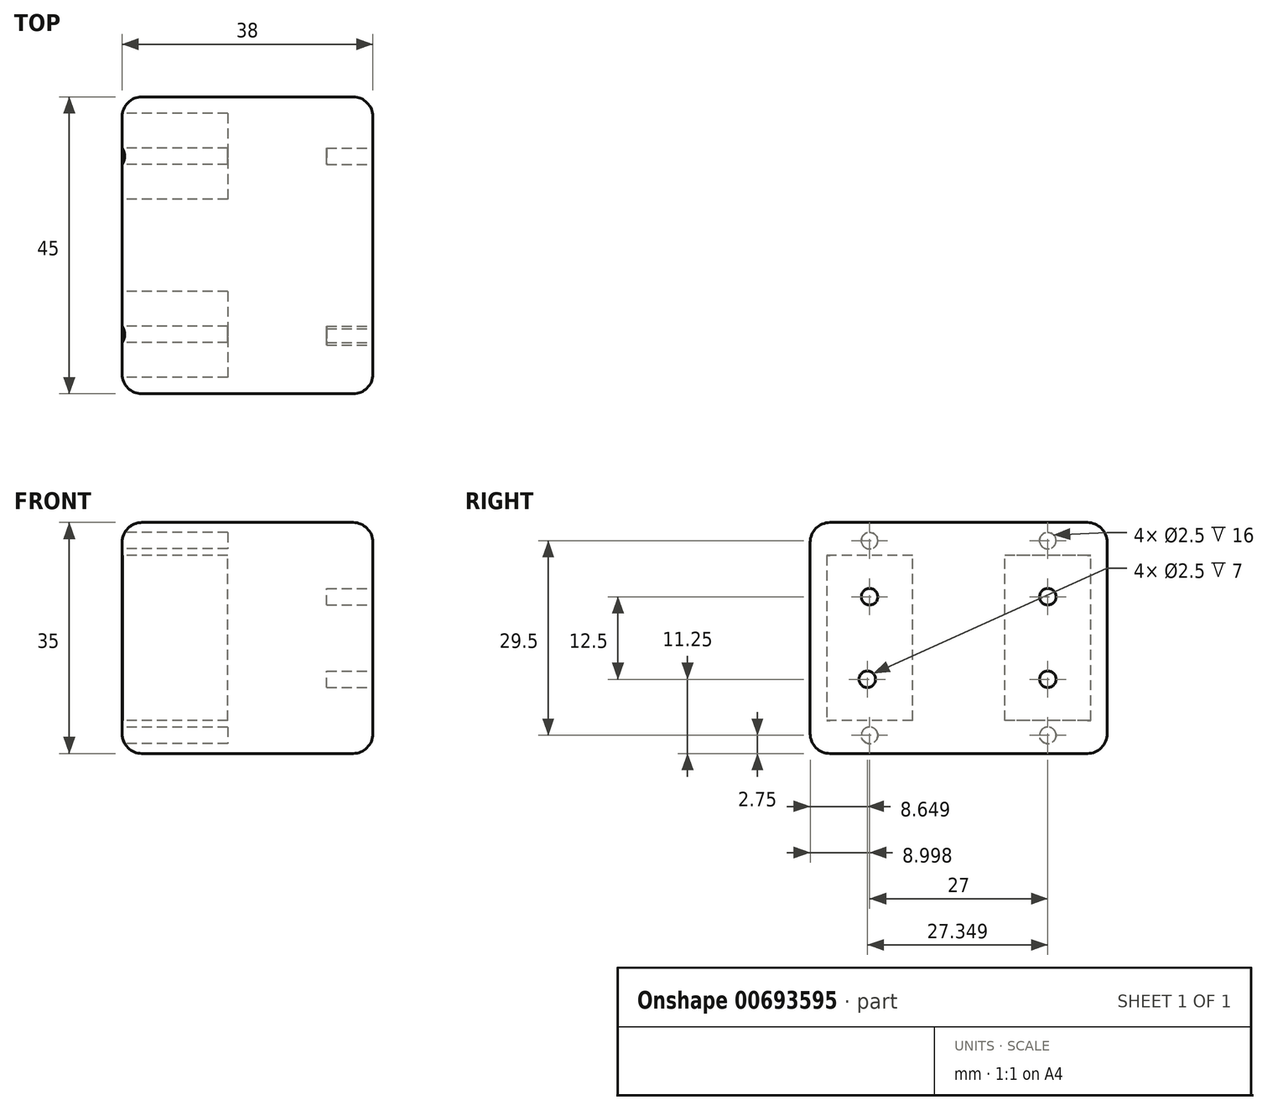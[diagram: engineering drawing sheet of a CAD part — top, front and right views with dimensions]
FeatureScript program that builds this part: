
annotation { "Feature Type Name" : "Feature", "Feature Type Description" : "" }
export const myFeature = defineFeature(function(context is Context, id is Id, definition is map)
    precondition{}
    {
        {
            var Q0;
            Q0=qCreatedBy(makeId("Top.planeOp"),FACE);
            var sketch = newSketch(context, id + "F0", { "sketchPlane" : qUnion([Q0])});
            skLineSegment(sketch, "E0.bottom", {"start": v(-14.13, 34.07) * mm, "end": v(23.87, 34.07) * mm});
            skLineSegment(sketch, "E0.top", {"start": v(-14.13, -10.93) * mm, "end": v(23.87, -10.93) * mm});
            skLineSegment(sketch, "E0.left", {"start": v(-14.13, 34.07) * mm, "end": v(-14.13, -10.93) * mm});
            skLineSegment(sketch, "E0.right", {"start": v(23.87, 34.07) * mm, "end": v(23.87, -10.93) * mm});
            skSolve(sketch);
        }
        {
            var Q0;
            Q0 = qSketchRegion(id + "F0", true);
            extrude(context, id + "F1", {"entities" : qUnion([Q0]), "depth" : 35 * mm, "offsetDistance" : 25 * mm});
        }
        {
            var Q0;
            Q0=makeQuery(id+"F1.opExtrude","SWEPT_FACE",FACE,{"disambiguationData":[OSD([sQuery(id+"F0.wireOp",EDGE,"E0.left")])]});
            var sketch = newSketch(context, id + "F2", { "sketchPlane" : qUnion([Q0])});
            skLineSegment(sketch, "E1.bottom", {"start": v(-31.57, 5) * mm, "end": v(-18.57, 5) * mm});
            skLineSegment(sketch, "E1.top", {"start": v(-31.57, 30) * mm, "end": v(-18.57, 30) * mm});
            skLineSegment(sketch, "E1.left", {"start": v(-31.57, 5) * mm, "end": v(-31.57, 30) * mm});
            skLineSegment(sketch, "E1.right", {"start": v(-18.57, 5) * mm, "end": v(-18.57, 30) * mm});
            skLineSegment(sketch, "E2.bottom", {"start": v(-4.57, 5) * mm, "end": v(8.43, 5) * mm});
            skLineSegment(sketch, "E2.top", {"start": v(-4.57, 30) * mm, "end": v(8.43, 30) * mm});
            skLineSegment(sketch, "E2.left", {"start": v(-4.57, 5) * mm, "end": v(-4.57, 30) * mm});
            skLineSegment(sketch, "E2.right", {"start": v(8.43, 5) * mm, "end": v(8.43, 30) * mm});
            skCircle(sketch, "E3", {"center": v(1.93, 32.25) * mm, "radius": 1.25 * mm});
            skCircle(sketch, "E4", {"center": v(1.93, 2.75) * mm, "radius": 1.25 * mm});
            skCircle(sketch, "E5", {"center": v(-25.07, 32.25) * mm, "radius": 1.25 * mm});
            skCircle(sketch, "E6", {"center": v(-25.07, 2.75) * mm, "radius": 1.25 * mm});
            skSolve(sketch);
        }
        {
            var Q0;
            Q0 = qSketchRegion(id + "F2", true);
            extrude(context, id + "F3", {"entities" : qUnion([Q0]), "operationType" : NewBodyOperationType.REMOVE, "oppositeDirection" : true, "depth" : 16 * mm, "offsetDistance" : 25 * mm});
        }
        {
            var Q0;
            Q0=makeQuery(id+"F1.opExtrude","CAP_EDGE",EDGE,{"disambiguationData":[OSD([sQuery(id+"F0.wireOp",EDGE,"E0.bottom")])],"isStart":true});
            var Q1;
            Q1=makeQuery(id+"F1.opExtrude","CAP_EDGE",EDGE,{"disambiguationData":[OSD([sQuery(id+"F0.wireOp",EDGE,"E0.bottom")])],"isStart":false});
            var Q2;
            Q2=makeQuery(id+"F1.opExtrude","CAP_EDGE",EDGE,{"disambiguationData":[OSD([sQuery(id+"F0.wireOp",EDGE,"E0.top")])],"isStart":true});
            var Q3;
            Q3=makeQuery(id+"F1.opExtrude","CAP_EDGE",EDGE,{"disambiguationData":[OSD([sQuery(id+"F0.wireOp",EDGE,"E0.top")])],"isStart":false});
            var Q4;
            Q4=makeQuery(id+"F1.opExtrude","CAP_EDGE",EDGE,{"disambiguationData":[OSD([sQuery(id+"F0.wireOp",EDGE,"E0.right")])],"isStart":false});
            var Q5;
            Q5=makeQuery(id+"F1.opExtrude","CAP_EDGE",EDGE,{"disambiguationData":[OSD([sQuery(id+"F0.wireOp",EDGE,"E0.right")])],"isStart":true});
            var Q6;
            Q6=makeQuery(id+"F1.opExtrude","SWEPT_EDGE",EDGE,{"disambiguationData":[OSD([sQuery(id+"F0.wireOp",EDGE,"E0.bottom"),sQuery(id+"F0.wireOp",EDGE,"E0.right")])]});
            var Q7;
            Q7=makeQuery(id+"F1.opExtrude","SWEPT_EDGE",EDGE,{"disambiguationData":[OSD([sQuery(id+"F0.wireOp",EDGE,"E0.top"),sQuery(id+"F0.wireOp",EDGE,"E0.right")])]});
            var Q8;
            Q8=makeQuery(id+"F1.opExtrude","CAP_EDGE",EDGE,{"disambiguationData":[OSD([sQuery(id+"F0.wireOp",EDGE,"E0.left")])],"isStart":false});
            var Q9;
            Q9=makeQuery(id+"F1.opExtrude","CAP_EDGE",EDGE,{"disambiguationData":[OSD([sQuery(id+"F0.wireOp",EDGE,"E0.left")])],"isStart":true});
            var Q10;
            Q10=makeQuery(id+"F1.opExtrude","SWEPT_EDGE",EDGE,{"disambiguationData":[OSD([sQuery(id+"F0.wireOp",EDGE,"E0.bottom"),sQuery(id+"F0.wireOp",EDGE,"E0.left")])]});
            var Q11;
            Q11=makeQuery(id+"F1.opExtrude","SWEPT_EDGE",EDGE,{"disambiguationData":[OSD([sQuery(id+"F0.wireOp",EDGE,"E0.top"),sQuery(id+"F0.wireOp",EDGE,"E0.left")])]});
            fillet(context, id + "F4", {"entities" : qUnion([Q0, Q1, Q2, Q3, Q4, Q5, Q6, Q7, Q8, Q9, Q10, Q11]), "radius" : 3 * mm, "tangentPropagation" : true, "allowEdgeOverflow" : false});
        }
        {
            var Q0;
            Q0=makeQuery(id+"F1.opExtrude","SWEPT_FACE",FACE,{"disambiguationData":[OSD([sQuery(id+"F0.wireOp",EDGE,"E0.right")])]});
            var sketch = newSketch(context, id + "F5", { "sketchPlane" : qUnion([Q0])});
            skCircle(sketch, "E7", {"center": v(-1.93, 23.75) * mm, "radius": 1.25 * mm});
            skCircle(sketch, "E8", {"center": v(-2.28, 11.25) * mm, "radius": 1.25 * mm});
            skCircle(sketch, "E9", {"center": v(25.07, 23.75) * mm, "radius": 1.25 * mm});
            skCircle(sketch, "E10", {"center": v(25.07, 11.25) * mm, "radius": 1.25 * mm});
            skSolve(sketch);
        }
        {
            var Q0;
            Q0 = qSketchRegion(id + "F5", true);
            extrude(context, id + "F6", {"entities" : qUnion([Q0]), "operationType" : NewBodyOperationType.REMOVE, "oppositeDirection" : true, "depth" : 7 * mm, "offsetDistance" : 25 * mm});
        }
    });
